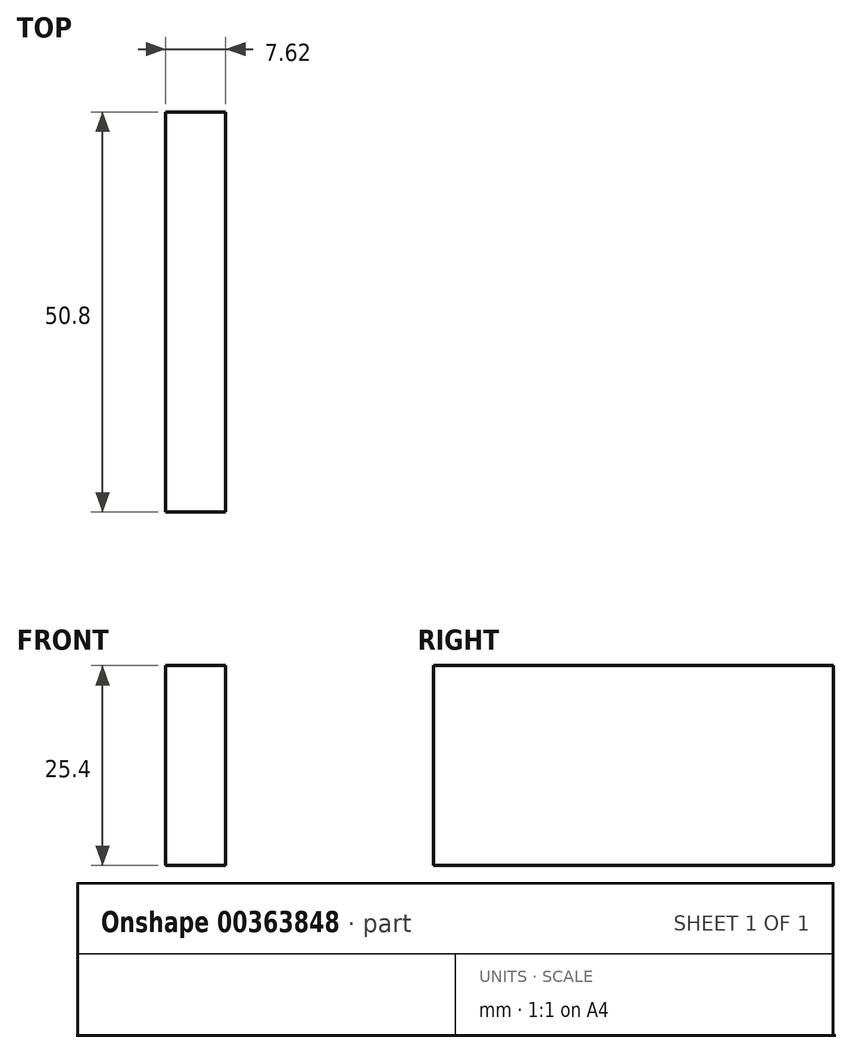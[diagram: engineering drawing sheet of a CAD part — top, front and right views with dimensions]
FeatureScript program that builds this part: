
annotation { "Feature Type Name" : "Feature", "Feature Type Description" : "" }
export const myFeature = defineFeature(function(context is Context, id is Id, definition is map)
    precondition{}
    {
        {
            var Q0;
            Q0=qCreatedBy(makeId("Right.planeOp"),FACE);
            var sketch = newSketch(context, id + "F0", { "sketchPlane" : qUnion([Q0])});
            skLineSegment(sketch, "E0.bottom", {"start": v(-24.06, 41.32) * mm, "end": v(26.74, 41.32) * mm});
            skLineSegment(sketch, "E0.top", {"start": v(-24.06, 15.92) * mm, "end": v(26.74, 15.92) * mm});
            skLineSegment(sketch, "E0.left", {"start": v(-24.06, 41.32) * mm, "end": v(-24.06, 15.92) * mm});
            skLineSegment(sketch, "E0.right", {"start": v(26.74, 41.32) * mm, "end": v(26.74, 15.92) * mm});
            skSolve(sketch);
        }
        {
            var Q0;
            Q0=makeQuery(id+"F0.imprint","IMPRINT",FACE,{"disambiguationData":[TD([[makeQuery(id+"F0.imprint","IMPRINT",EDGE,{"derivedFrom":sQuery(id+"F0.wireOp",EDGE,"E0.bottom")}),-1.0]])]});
            extrude(context, id + "F1", {"entities" : qUnion([Q0]), "depth" : 7.62 * mm});
        }
    });
